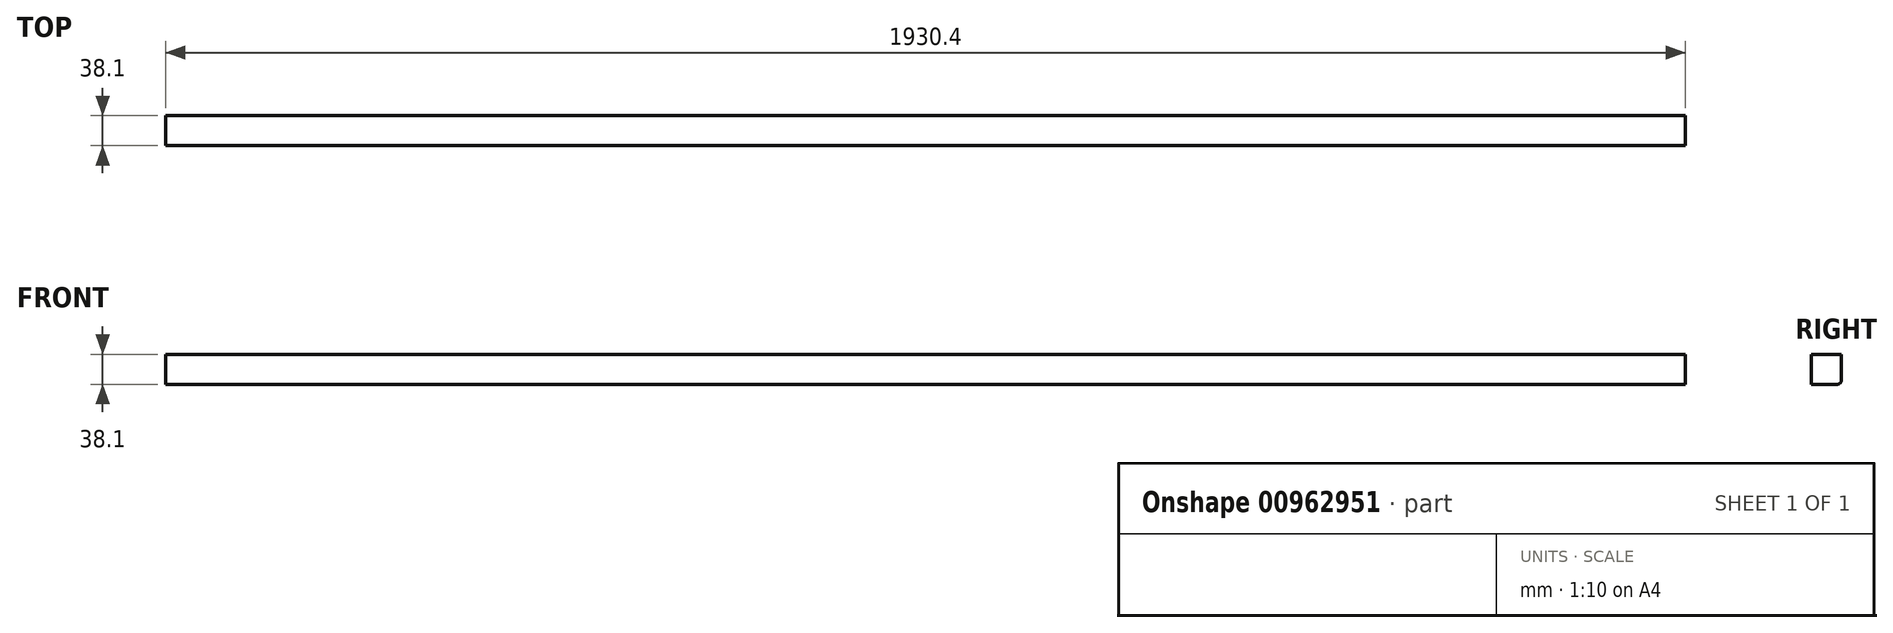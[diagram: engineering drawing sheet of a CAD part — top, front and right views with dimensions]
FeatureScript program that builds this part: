
annotation { "Feature Type Name" : "Feature", "Feature Type Description" : "" }
export const myFeature = defineFeature(function(context is Context, id is Id, definition is map)
    precondition{}
    {
        {
            var Q0;
            Q0=qCreatedBy(makeId("Right.planeOp"),FACE);
            var sketch = newSketch(context, id + "F0", { "sketchPlane" : qUnion([Q0])});
            skLineSegment(sketch, "E0.bottom", {"start": v(-64.95, 36.18) * mm, "end": v(-26.85, 36.18) * mm});
            skLineSegment(sketch, "E0.top", {"start": v(-64.95, -1.92) * mm, "end": v(-26.85, -1.92) * mm});
            skLineSegment(sketch, "E0.left", {"start": v(-64.95, 36.18) * mm, "end": v(-64.95, -1.92) * mm});
            skLineSegment(sketch, "E0.right", {"start": v(-26.85, 36.18) * mm, "end": v(-26.85, -1.92) * mm});
            skSolve(sketch);
        }
        {
            var Q0;
            Q0=makeQuery(id+"F0.imprint","IMPRINT",FACE,{"disambiguationData":[TD([[makeQuery(id+"F0.imprint","IMPRINT",EDGE,{"derivedFrom":sQuery(id+"F0.wireOp",EDGE,"E0.bottom")}),-1.0]])]});
            extrude(context, id + "F1", {"entities" : qUnion([Q0]), "depth" : 1930.4 * mm, "offsetDistance" : 25.4 * mm});
        }
        {
            var Q0;
            Q0=makeQuery(id+"F1.opExtrude","SWEPT_EDGE",EDGE,{"disambiguationData":[OSD([sQuery(id+"F0.wireOp",EDGE,"E0.top"),sQuery(id+"F0.wireOp",EDGE,"E0.right")])]});
            fillet(context, id + "F2", {"entities" : qUnion([Q0]), "radius" : 5.08 * mm, "tangentPropagation" : true, "allowEdgeOverflow" : false});
        }
    });
